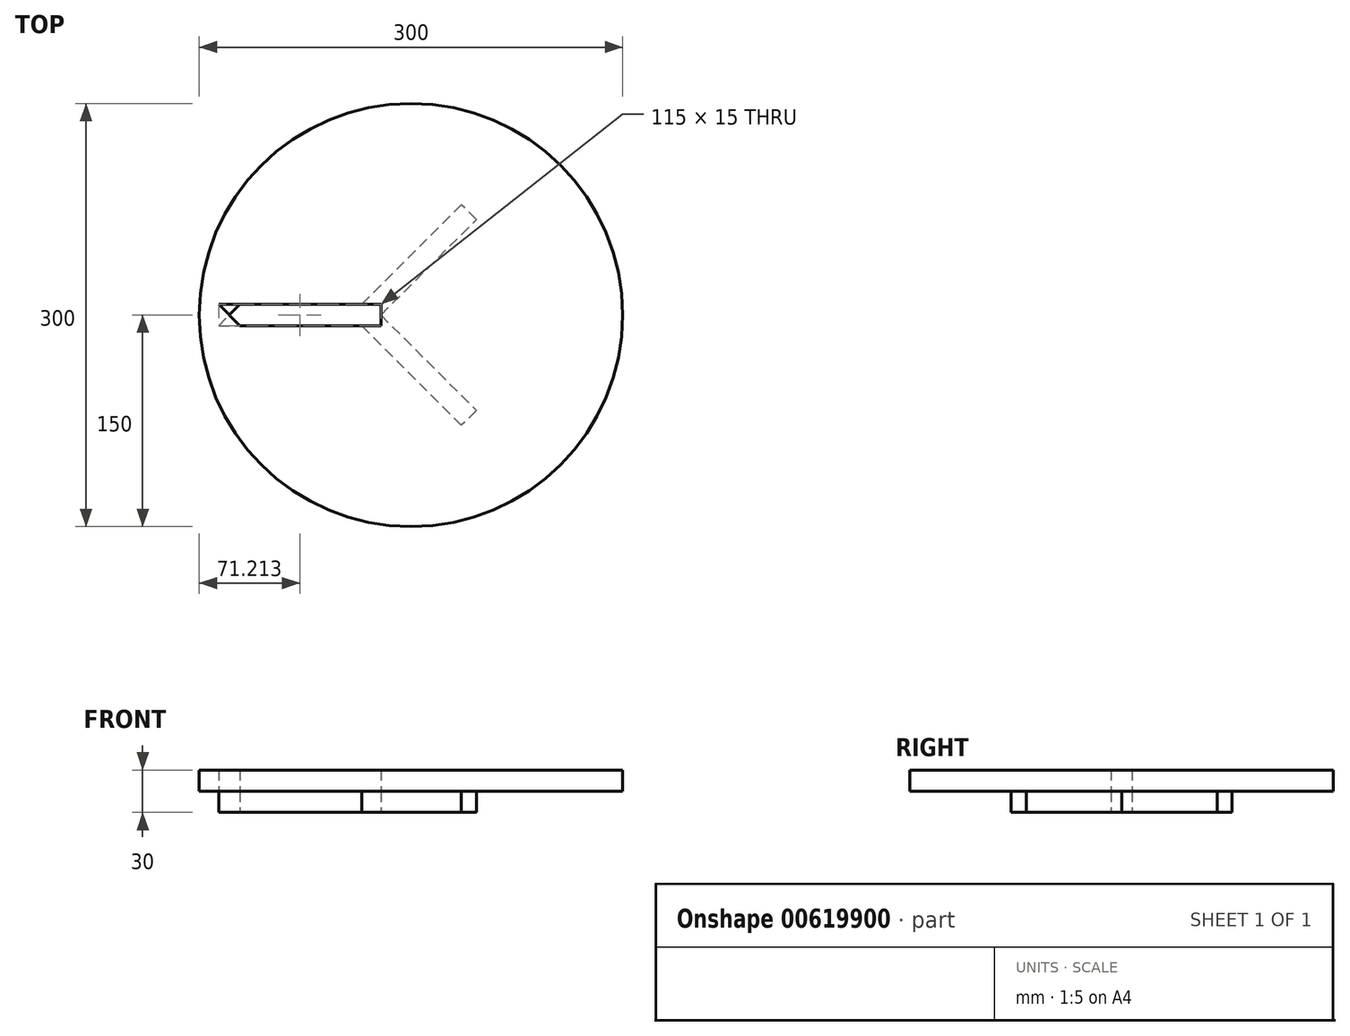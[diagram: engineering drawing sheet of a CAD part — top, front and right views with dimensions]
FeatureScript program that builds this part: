
annotation { "Feature Type Name" : "Feature", "Feature Type Description" : "" }
export const myFeature = defineFeature(function(context is Context, id is Id, definition is map)
    precondition{}
    {
        {
            var Q0;
            Q0=qCreatedBy(makeId("Top.planeOp"),FACE);
            var sketch = newSketch(context, id + "F0", { "sketchPlane" : qUnion([Q0])});
            skLineSegment(sketch, "E0", {"start": v(0, 0) * mm, "end": v(141.42, 141.42) * mm});
            skLineSegment(sketch, "E1", {"start": v(0, 0) * mm, "end": v(141.42, -141.42) * mm});
            skLineSegment(sketch, "E2", {"start": v(141.42, -141.42) * mm, "end": v(152.03, -130.81) * mm});
            skLineSegment(sketch, "E3", {"start": v(152.03, -130.81) * mm, "end": v(21.21, 0) * mm});
            skLineSegment(sketch, "E4", {"start": v(21.21, 0) * mm, "end": v(152.03, 130.81) * mm});
            skLineSegment(sketch, "E5", {"start": v(152.03, 130.81) * mm, "end": v(141.42, 141.42) * mm});
            skLineSegment(sketch, "E6", {"start": v(21.21, 0) * mm, "end": v(10.6, 10.6) * mm});
            skLineSegment(sketch, "E7", {"start": v(21.21, 0) * mm, "end": v(10.6, -10.6) * mm});
            skLineSegment(sketch, "E8", {"start": v(10.6, -10.6) * mm, "end": v(0, 0) * mm});
            skLineSegment(sketch, "E9", {"start": v(0, 0) * mm, "end": v(10.6, 10.6) * mm});
            skLineSegment(sketch, "E10.right", {"start": v(128.71, 7.5) * mm, "end": v(128.71, -7.5) * mm});
            skLineSegment(sketch, "E11.trimOffspring", {"start": v(28.71, 7.5) * mm, "end": v(128.71, 7.5) * mm});
            skLineSegment(sketch, "E12.trimOffspring", {"start": v(28.71, -7.5) * mm, "end": v(128.71, -7.5) * mm});
            skLineSegment(sketch, "E13", {"start": v(28.71, 7.5) * mm, "end": v(21.21, 0) * mm});
            skLineSegment(sketch, "E14", {"start": v(21.21, 0) * mm, "end": v(28.71, -7.5) * mm});
            skPoint(sketch, "E15.orphan", {"position": v(0, 7.5) * mm});
            skPoint(sketch, "E10.left.end.orphan", {"position": v(0, -7.5) * mm});
            skLineSegment(sketch, "E16", {"start": v(28.71, 7.5) * mm, "end": v(13.71, 7.5) * mm});
            skLineSegment(sketch, "E17", {"start": v(13.71, 7.5) * mm, "end": v(28.71, -7.5) * mm});
            skLineSegment(sketch, "E18", {"start": v(13.71, -7.5) * mm, "end": v(28.71, -7.5) * mm});
            skLineSegment(sketch, "E19", {"start": v(0, 0) * mm, "end": v(306.37, 0) * mm, "construction": true});
            skPoint(sketch, "E19.endSnap0", {"position": v(128.71, 0) * mm});
            skLineSegment(sketch, "E20", {"start": v(128.71, 0) * mm, "end": v(196.32, 67.6) * mm});
            skLineSegment(sketch, "E21", {"start": v(196.32, 67.6) * mm, "end": v(185.71, 78.21) * mm});
            skLineSegment(sketch, "E22", {"start": v(185.71, 78.21) * mm, "end": v(115, 7.5) * mm});
            skLineSegment(sketch, "E23", {"start": v(128.71, 0) * mm, "end": v(196.32, -67.6) * mm});
            skLineSegment(sketch, "E24", {"start": v(196.32, -67.6) * mm, "end": v(185.71, -78.21) * mm});
            skLineSegment(sketch, "E25", {"start": v(185.71, -78.21) * mm, "end": v(115, -7.5) * mm});
            skCircle(sketch, "E26", {"center": v(150, 0) * mm, "radius": 150 * mm});
            skSolve(sketch);
        }
        {
            var Q0;
            {var subQ5=sQuery(id+"F0.wireOp",EDGE,"E6");Q0=makeQuery(id+"F0.imprint","IMPRINT",FACE,{"disambiguationData":[TD([[makeQuery(id+"F0.imprint","IMPRINT",EDGE,{"derivedFrom":subQ5}),1.0]])]});}
            var Q1;
            Q1=sQuery(id+"F0.wireOp",EDGE,"E9");
            var Q2;
            Q2=sQuery(id+"F0.wireOp",EDGE,"E6");
            var Q3;
            Q3=sQuery(id+"F0.wireOp",EDGE,"E7");
            var Q4;
            Q4=sQuery(id+"F0.wireOp",EDGE,"E8");
            extrude(context, id + "F1", {"entities" : qUnion([Q0]), "surfaceEntities" : qUnion([Q1, Q2, Q3, Q4]), "depth" : 550 * mm, "offsetDistance" : 25 * mm});
        }
        {
            var Q0;
            Q0=makeQuery(id+"F0.imprint","IMPRINT",FACE,{"disambiguationData":[TD([[makeQuery(id+"F0.imprint","IMPRINT",EDGE,{"derivedFrom":sQuery(id+"F0.wireOp",EDGE,"E0")}),-1.0]])]});
            var Q1;
            Q1=makeQuery(id+"F0.imprint","IMPRINT",FACE,{"disambiguationData":[TD([[makeQuery(id+"F0.imprint","IMPRINT",EDGE,{"derivedFrom":sQuery(id+"F0.wireOp",EDGE,"E1")}),1.0]])]});
            var Q2;
            {var subQ0=sQuery(id+"F0.wireOp",EDGE,"E13");Q2=makeQuery(id+"F0.imprint","IMPRINT",FACE,{"disambiguationData":[TD([[makeQuery(id+"F0.imprint","IMPRINT",EDGE,{"derivedFrom":subQ0}),-1.0]])]});}
            var Q3;
            {var subQ3=sQuery(id+"F0.wireOp",EDGE,"E18");Q3=makeQuery(id+"F0.imprint","IMPRINT",FACE,{"disambiguationData":[TD([[makeQuery(id+"F0.imprint","IMPRINT",EDGE,{"derivedFrom":subQ3}),1.0]])]});}
            extrude(context, id + "F2", {"entities" : qUnion([Q0, Q1, Q2, Q3]), "depth" : 15 * mm, "offsetDistance" : 25 * mm});
        }
        {
            var Q0;
            Q0=makeQuery(id+"F0.imprint","IMPRINT",FACE,{"disambiguationData":[TD([[makeQuery(id+"F0.imprint","IMPRINT",EDGE,{"derivedFrom":sQuery(id+"F0.wireOp",EDGE,"E10.right")}),-1.0]])]});
            var Q1;
            {var subQ0=sQuery(id+"F0.wireOp",EDGE,"E13");Q1=makeQuery(id+"F0.imprint","IMPRINT",FACE,{"disambiguationData":[TD([[makeQuery(id+"F0.imprint","IMPRINT",EDGE,{"derivedFrom":subQ0}),-1.0]])]});}
            var Q2;
            {var subQ3=sQuery(id+"F0.wireOp",EDGE,"E18");Q2=makeQuery(id+"F0.imprint","IMPRINT",FACE,{"disambiguationData":[TD([[makeQuery(id+"F0.imprint","IMPRINT",EDGE,{"derivedFrom":subQ3}),1.0]])]});}
            var Q3;
            {var subQ0=sQuery(id+"F0.wireOp",EDGE,"E20");Q3=makeQuery(id+"F0.imprint","IMPRINT",FACE,{"disambiguationData":[TD([[makeQuery(id+"F0.imprint","IMPRINT",EDGE,{"derivedFrom":subQ0}),1.0]])]});}
            var Q4;
            {var subQ0=sQuery(id+"F0.wireOp",EDGE,"E23");Q4=makeQuery(id+"F0.imprint","IMPRINT",FACE,{"disambiguationData":[TD([[makeQuery(id+"F0.imprint","IMPRINT",EDGE,{"derivedFrom":subQ0}),-1.0]])]});}
            extrude(context, id + "F3", {"entities" : qUnion([Q0, Q1, Q2, Q3, Q4]), "depth" : 550 * mm, "offsetDistance" : 25 * mm});
        }
        {
            var Q0;
            Q0=makeQuery(id+"F3.opExtrude","CAP_FACE",FACE,{"disambiguationData":[OSD([sQuery(id+"F0.wireOp",EDGE,"E7"),sQuery(id+"F0.wireOp",EDGE,"E11.trimOffspring"),sQuery(id+"F0.wireOp",EDGE,"E12.trimOffspring"),sQuery(id+"F0.wireOp",EDGE,"E16"),sQuery(id+"F0.wireOp",EDGE,"E17"),sQuery(id+"F0.wireOp",EDGE,"E18"),sQuery(id+"F0.wireOp",EDGE,"E20"),sQuery(id+"F0.wireOp",EDGE,"E21"),sQuery(id+"F0.wireOp",EDGE,"E22"),sQuery(id+"F0.wireOp",EDGE,"E23"),sQuery(id+"F0.wireOp",EDGE,"E24"),sQuery(id+"F0.wireOp",EDGE,"E25")])],"isStart":false});
            extrude(context, id + "F4", {"entities" : qUnion([Q0]), "operationType" : NewBodyOperationType.INTERSECT, "oppositeDirection" : true, "depth" : 15 * mm, "offsetDistance" : 25 * mm});
        }
        {
            var Q0;
            Q0=makeQuery(id+"F0.imprint","IMPRINT",FACE,{"disambiguationData":[TD([[makeQuery(id+"F0.imprint","IMPRINT",EDGE,{"derivedFrom":sQuery(id+"F0.wireOp",EDGE,"E0")}),1.0]])]});
            var Q1;
            {var subQ0=sQuery(id+"F0.wireOp",EDGE,"E20");Q1=makeQuery(id+"F0.imprint","IMPRINT",FACE,{"disambiguationData":[TD([[makeQuery(id+"F0.imprint","IMPRINT",EDGE,{"derivedFrom":subQ0}),1.0]])]});}
            var Q2;
            {var subQ0=sQuery(id+"F0.wireOp",EDGE,"E23");Q2=makeQuery(id+"F0.imprint","IMPRINT",FACE,{"disambiguationData":[TD([[makeQuery(id+"F0.imprint","IMPRINT",EDGE,{"derivedFrom":subQ0}),-1.0]])]});}
            var Q3;
            {var subQ4=sQuery(id+"F0.wireOp",EDGE,"E13");Q3=makeQuery(id+"F0.imprint","IMPRINT",FACE,{"disambiguationData":[TD([[makeQuery(id+"F0.imprint","IMPRINT",EDGE,{"derivedFrom":subQ4}),1.0]])]});}
            var Q4;
            {var subQ1=sQuery(id+"F0.wireOp",EDGE,"E1");Q4=makeQuery(id+"F0.imprint","IMPRINT",FACE,{"disambiguationData":[TD([[makeQuery(id+"F0.imprint","IMPRINT",EDGE,{"derivedFrom":subQ1}),1.0]])]});}
            var Q5;
            Q5=makeQuery(id+"F0.imprint","IMPRINT",FACE,{"disambiguationData":[TD([[makeQuery(id+"F0.imprint","IMPRINT",EDGE,{"derivedFrom":sQuery(id+"F0.wireOp",EDGE,"E0")}),-1.0]])]});
            var Q6;
            {var subQ4=sQuery(id+"F0.wireOp",EDGE,"E6");Q6=makeQuery(id+"F0.imprint","IMPRINT",FACE,{"disambiguationData":[TD([[makeQuery(id+"F0.imprint","IMPRINT",EDGE,{"derivedFrom":subQ4}),1.0]])]});}
            var Q7;
            {var subQ3=sQuery(id+"F0.wireOp",EDGE,"E18");Q7=makeQuery(id+"F0.imprint","IMPRINT",FACE,{"disambiguationData":[TD([[makeQuery(id+"F0.imprint","IMPRINT",EDGE,{"derivedFrom":subQ3}),1.0]])]});}
            var Q8;
            {var subQ0=sQuery(id+"F0.wireOp",EDGE,"E13");Q8=makeQuery(id+"F0.imprint","IMPRINT",FACE,{"disambiguationData":[TD([[makeQuery(id+"F0.imprint","IMPRINT",EDGE,{"derivedFrom":subQ0}),-1.0]])]});}
            extrude(context, id + "F5", {"entities" : qUnion([Q0, Q1, Q2, Q3, Q4, Q5, Q6, Q7, Q8]), "depth" : 565 * mm, "offsetDistance" : 25 * mm, "hasSecondDirection" : true, "secondDirectionOppositeDirection" : false, "secondDirectionDepth" : 550 * mm});
        }
    });
